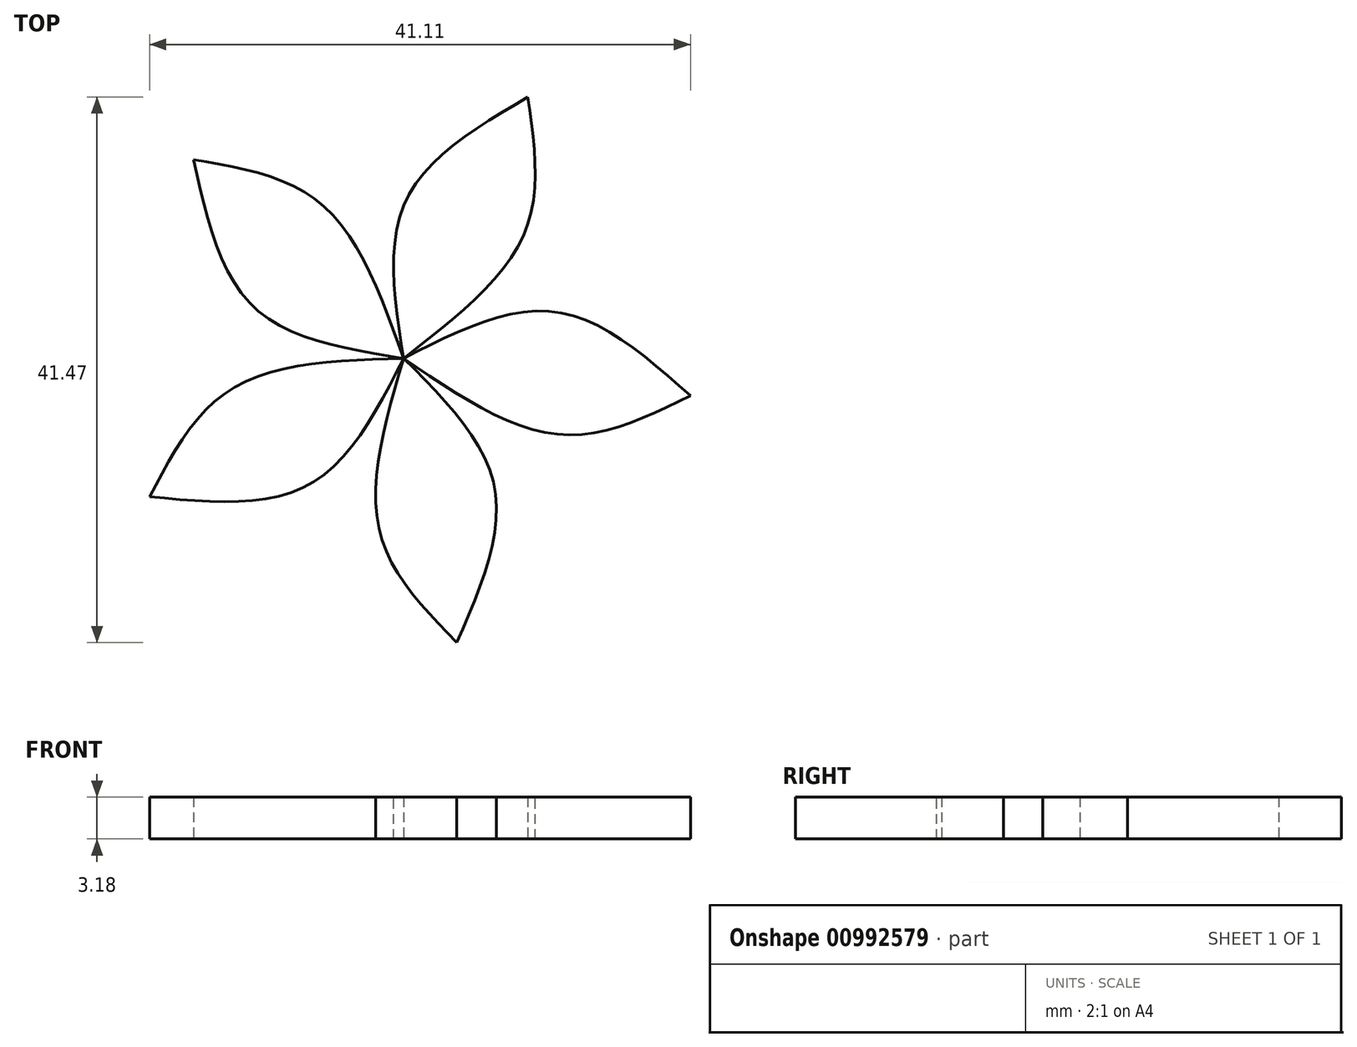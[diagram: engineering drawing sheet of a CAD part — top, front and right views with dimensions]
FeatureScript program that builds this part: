
annotation { "Feature Type Name" : "Feature", "Feature Type Description" : "" }
export const myFeature = defineFeature(function(context is Context, id is Id, definition is map)
    precondition{}
    {
        {
            var Q0;
            Q0=qCreatedBy(makeId("Top.planeOp"),FACE);
            var sketch = newSketch(context, id + "F0", { "sketchPlane" : qUnion([Q0])});
            skFitSpline(sketch, "E0", {"points": [v(0, 0) * mm, v(-11.37, 3.89) * mm, v(-15.97, 15.1) * mm], "startDerivative": vector(-26.19, 4.15) * mm, "endDerivative": vector(-5.78, 26.05) * mm});
            skFitSpline(sketch, "E1", {"points": [v(-15.97, 15.1) * mm, v(-6.19, 11.66) * mm, v(0, 0) * mm], "startDerivative": vector(22.97, -3.9) * mm, "endDerivative": vector(9.25, -25.87) * mm});
            skSolve(sketch);
        }
        {
            var Q0;
            Q0=makeQuery(id+"F0.imprint","IMPRINT",FACE,{"disambiguationData":[TD([[makeQuery(id+"F0.imprint","IMPRINT",EDGE,{"derivedFrom":sQuery(id+"F0.wireOp",EDGE,"E0")}),-1.0]])]});
            extrude(context, id + "F1", {"entities" : qUnion([Q0]), "depth" : 3.17 * mm, "offsetDistance" : 25.4 * mm});
        }
        {
            var Q0;
            Q0=makeQuery(id+"F1.opExtrude","SWEPT_BODY",BODY,{"disambiguationData":[OSD([sQuery(id+"F0.wireOp",EDGE,"E0"),sQuery(id+"F0.wireOp",EDGE,"E1")])]});
            var Q1;
            {var subQ0=sQuery(id+"F0.wireOp",EDGE,"E1");var subQ1=sQuery(id+"F0.wireOp",EDGE,"E0");Q1=makeQuery(id+"F1.opExtrude","SWEPT_EDGE",EDGE,{"disambiguationData":[OSD([subQ1,subQ0]),TDD([makeQuery(id+"F0.imprint","INTERSECT",VERTEX,{"disambiguationData":[OD(0.0)],"derivedFrom":[subQ1,subQ0]})])]});}
            circularPattern(context, id + "F2", {"entities" : qUnion([Q0]), "axis" : qUnion([Q1]), "angle" : 360 * degree, "instanceCount" : 5, "equalSpace" : true});
        }
    });
